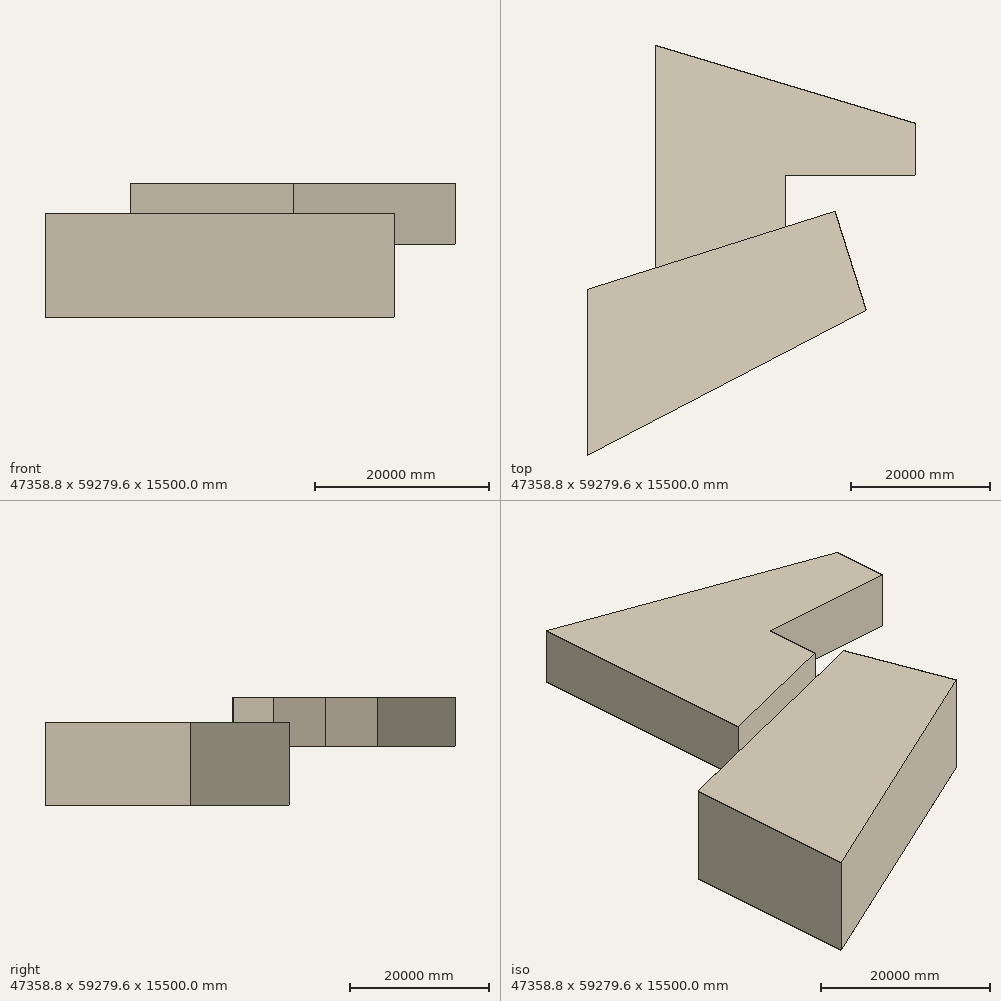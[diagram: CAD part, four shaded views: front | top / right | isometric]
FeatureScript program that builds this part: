
annotation { "Feature Type Name" : "Feature", "Feature Type Description" : "" }
export const myFeature = defineFeature(function(context is Context, id is Id, definition is map)
    precondition{}
    {
        {
            var Q0;
            Q0=qCreatedBy(makeId("Top.planeOp"),FACE);
            var sketch = newSketch(context, id + "F0", { "sketchPlane" : qUnion([Q0])});
            skLineSegment(sketch, "E0", {"start": v(0, 18750) * mm, "end": v(0, 0) * mm});
            skLineSegment(sketch, "E1", {"start": v(0, 0) * mm, "end": v(37500, 0) * mm});
            skLineSegment(sketch, "E2", {"start": v(37500, 0) * mm, "end": v(37500, 7500) * mm});
            skLineSegment(sketch, "E3", {"start": v(37500, 7500) * mm, "end": v(0, 18750) * mm});
            skLineSegment(sketch, "E4", {"start": v(0, 0) * mm, "end": v(0, -15740.77) * mm, "construction": true});
            skLineSegment(sketch, "E5", {"start": v(0, -15740.77) * mm, "end": v(18750, -7500) * mm, "construction": true});
            skLineSegment(sketch, "E6", {"start": v(18750, -7500) * mm, "end": v(18750, 0) * mm, "construction": true});
            skSolve(sketch);
        }
        {
            var Q0;
            Q0 = qSketchRegion(id + "F0", true);
            extrude(context, id + "F1", {"entities" : qUnion([Q0]), "depth" : 7000 * mm});
        }
        {
            var Q0;
            Q0=qCreatedBy(makeId("Top.planeOp"),FACE);
            var sketch = newSketch(context, id + "F2", { "sketchPlane" : qUnion([Q0])});
            skLineSegment(sketch, "E7", {"start": v(0, 0) * mm, "end": v(0, -13417.94) * mm});
            skLineSegment(sketch, "E8", {"start": v(0, -13417.94) * mm, "end": v(18750, -7500) * mm});
            skLineSegment(sketch, "E9", {"start": v(18750, -7500) * mm, "end": v(18750, 0) * mm});
            skLineSegment(sketch, "E10", {"start": v(18750, 0) * mm, "end": v(0, 0) * mm});
            skSolve(sketch);
        }
        {
            var Q0;
            Q0 = qSketchRegion(id + "F2", true);
            extrude(context, id + "F3", {"entities" : qUnion([Q0]), "operationType" : NewBodyOperationType.ADD, "depth" : 7000 * mm});
        }
        {
            var Q0;
            Q0=qCreatedBy(makeId("Top.planeOp"),FACE);
            cPlane(context, id + "F4", {"entities" : qUnion([Q0]), "cplaneType" : CPlaneType.OFFSET, "offset" : 8500 * mm, "oppositeDirection" : true, "width" : 152.4 * mm, "height" : 152.4 * mm});
        }
        {
            var Q0;
            Q0=qCreatedBy(id+"F4.planeOp",FACE);
            var sketch = newSketch(context, id + "F5", { "sketchPlane" : qUnion([Q0])});
            skLineSegment(sketch, "E11", {"start": v(25902.21, -5242.6) * mm, "end": v(30417.02, -19547.01) * mm});
            skLineSegment(sketch, "E12", {"start": v(30417.02, -19547.01) * mm, "end": v(-9858.84, -40529.63) * mm});
            skLineSegment(sketch, "E13", {"start": v(-9858.84, -40529.63) * mm, "end": v(-9858.84, -16529.63) * mm});
            skLineSegment(sketch, "E14", {"start": v(25902.21, -5242.6) * mm, "end": v(-9858.84, -16529.63) * mm});
            skSolve(sketch);
        }
        {
            var Q0;
            Q0 = qSketchRegion(id + "F5", true);
            extrude(context, id + "F6", {"entities" : qUnion([Q0]), "operationType" : NewBodyOperationType.ADD, "depth" : 12000 * mm});
        }
        {
            var Q0;
            Q0=qCreatedBy(makeId("Top.planeOp"),FACE);
            cPlane(context, id + "F7", {"entities" : qUnion([Q0]), "cplaneType" : CPlaneType.OFFSET, "offset" : 200 * mm, "width" : 150 * mm, "height" : 150 * mm});
        }
        {
            var Q0;
            Q0=qCreatedBy(id+"F7.planeOp",FACE);
            var sketch = newSketch(context, id + "F8", { "sketchPlane" : qUnion([Q0])});
            skLineSegment(sketch, "E15.0", {"start": v(37300, 200) * mm, "end": v(37300, 7351.2) * mm});
            skLineSegment(sketch, "E15.1", {"start": v(200, 18481.2) * mm, "end": v(200, -13145.1) * mm});
            skLineSegment(sketch, "E15.2", {"start": v(200, -13145.1) * mm, "end": v(18550, -7353.4) * mm});
            skLineSegment(sketch, "E15.3", {"start": v(37300, 7351.2) * mm, "end": v(200, 18481.2) * mm});
            skLineSegment(sketch, "E15.4", {"start": v(18550, -7353.4) * mm, "end": v(18550, 200) * mm});
            skLineSegment(sketch, "E15.5", {"start": v(18550, 200) * mm, "end": v(37300, 200) * mm});
            skSolve(sketch);
        }
        {
            var Q0;
            Q0 = qSketchRegion(id + "F8", true);
            extrude(context, id + "F9", {"entities" : qUnion([Q0]), "operationType" : NewBodyOperationType.REMOVE, "depth" : 3200 * mm});
        }
        {
            var Q0;
            Q0=qCreatedBy(makeId("Top.planeOp"),FACE);
            cPlane(context, id + "F10", {"entities" : qUnion([Q0]), "cplaneType" : CPlaneType.OFFSET, "offset" : 3600 * mm, "width" : 150 * mm, "height" : 150 * mm});
        }
        {
            var Q0;
            Q0=qCreatedBy(id+"F10.planeOp",FACE);
            var sketch = newSketch(context, id + "F11", { "sketchPlane" : qUnion([Q0])});
            skLineSegment(sketch, "E16.0", {"start": v(37300, 7351.2) * mm, "end": v(200, 18481.2) * mm});
            skLineSegment(sketch, "E17.0", {"start": v(37300, 200) * mm, "end": v(37300, 7351.2) * mm});
            skLineSegment(sketch, "E18.0", {"start": v(18550, 200) * mm, "end": v(37300, 200) * mm});
            skLineSegment(sketch, "E19.0", {"start": v(18550, -7353.4) * mm, "end": v(18550, 200) * mm});
            skLineSegment(sketch, "E20.0", {"start": v(200, -13145.1) * mm, "end": v(18550, -7353.4) * mm});
            skLineSegment(sketch, "E21.0", {"start": v(200, 18481.2) * mm, "end": v(200, -13145.1) * mm});
            skSolve(sketch);
        }
        {
            var Q0;
            Q0 = qSketchRegion(id + "F11", true);
            extrude(context, id + "F12", {"entities" : qUnion([Q0]), "operationType" : NewBodyOperationType.REMOVE, "depth" : 3200 * mm});
        }
        {
            var Q0;
            Q0=qCreatedBy(id+"F10.planeOp",FACE);
            var sketch = newSketch(context, id + "F13", { "sketchPlane" : qUnion([Q0])});
            skCircle(sketch, "E22", {"center": v(8804.61, 8680.06) * mm, "radius": 3500 * mm});
            skSolve(sketch);
        }
        {
            var Q0;
            Q0 = qSketchRegion(id + "F13", true);
            extrude(context, id + "F14", {"entities" : qUnion([Q0]), "operationType" : NewBodyOperationType.REMOVE, "oppositeDirection" : true, "depth" : 25 * mm});
        }
        {
            var Q0;
            Q0=makeQuery(id+"F6.opExtrude","CAP_FACE",FACE,{"disambiguationData":[OSD([sQuery(id+"F5.wireOp",EDGE,"E11"),sQuery(id+"F5.wireOp",EDGE,"E12"),sQuery(id+"F5.wireOp",EDGE,"E13"),sQuery(id+"F5.wireOp",EDGE,"E14")])],"isStart":true});
            cPlane(context, id + "F15", {"entities" : qUnion([Q0]), "cplaneType" : CPlaneType.OFFSET, "offset" : 200 * mm, "oppositeDirection" : true, "width" : 150 * mm, "height" : 150 * mm});
        }
        {
            var Q0;
            Q0=qCreatedBy(id+"F15.planeOp",FACE);
            var sketch = newSketch(context, id + "F16", { "sketchPlane" : qUnion([Q0])});
            skLineSegment(sketch, "E23.0", {"start": v(30175.79, 19447.18) * mm, "end": v(-9658.84, 40199.92) * mm});
            skLineSegment(sketch, "E23.1", {"start": v(60.2, 13608.67) * mm, "end": v(-9658.84, 16676.23) * mm});
            skLineSegment(sketch, "E23.2", {"start": v(60.2, 13608.67) * mm, "end": v(18810.2, 7690.73) * mm});
            skLineSegment(sketch, "E23.3", {"start": v(-9658.84, 40199.92) * mm, "end": v(-9658.84, 16676.23) * mm});
            skLineSegment(sketch, "E23.4", {"start": v(25771.68, 5493.52) * mm, "end": v(18810.2, 7690.73) * mm});
            skLineSegment(sketch, "E23.5", {"start": v(25771.68, 5493.52) * mm, "end": v(30175.79, 19447.18) * mm});
            skSolve(sketch);
        }
        {
            var Q0;
            Q0 = qSketchRegion(id + "F16", true);
            extrude(context, id + "F17", {"entities" : qUnion([Q0]), "operationType" : NewBodyOperationType.REMOVE, "oppositeDirection" : true, "depth" : 11600 * mm});
        }
        {
            var Q0;
            Q0=qCreatedBy(id+"F15.planeOp",FACE);
            var sketch = newSketch(context, id + "F18", { "sketchPlane" : qUnion([Q0])});
            skLineSegment(sketch, "E24", {"start": v(8757.14, 10863.7) * mm, "end": v(8757.14, 30605.7) * mm});
            skLineSegment(sketch, "E25", {"start": v(8757.14, 30605.7) * mm, "end": v(18550, 25503.9) * mm});
            skLineSegment(sketch, "E26", {"start": v(18550, 25503.9) * mm, "end": v(18550, 7772.85) * mm});
            skLineSegment(sketch, "E27", {"start": v(18550, 7772.85) * mm, "end": v(8757.14, 10863.7) * mm});
            skSolve(sketch);
        }
        {
            var Q0;
            Q0 = qSketchRegion(id + "F18", true);
            extrude(context, id + "F19", {"entities" : qUnion([Q0]), "operationType" : NewBodyOperationType.ADD, "oppositeDirection" : true, "depth" : 8500 * mm});
        }
    });
